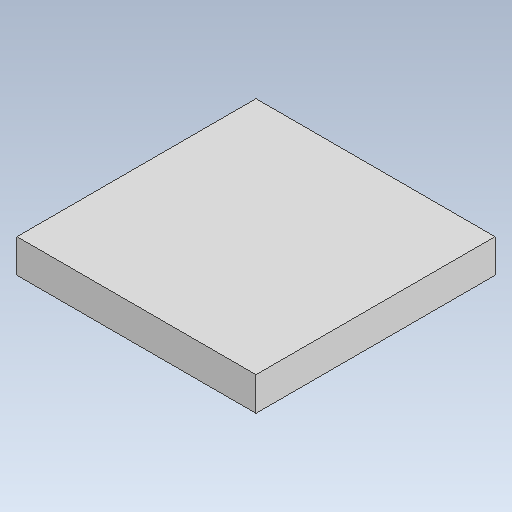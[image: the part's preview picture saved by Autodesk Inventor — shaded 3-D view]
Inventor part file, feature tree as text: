
AUTODESK INVENTOR PART (.ipt)
format: ipt  version: 2021.1 (Build 251245000, 245)  size: 143,872 bytes
history: native  units: mm
features: extrude x3, sketch x3, fillet x2
ambient origin geometry x8: Origin, YZ Plane, XZ Plane, XY Plane, X Axis, Y Axis, Z Axis, Center Point
bodies: Solid1 (feature_tree)
feature tree (8):
  extrude  "Extrusion1"  Depth=2.0mm TaperAngle=0.0deg
  extrude  "Extrusion2"  Depth=0.3mm
  extrude  "Extrusion3"  [1 undecoded]
  fillet  "Fillet1"  [1 undecoded]
  fillet  "Fillet2"  [1 undecoded]
  sketch  "Sketch1"  dims[d0=5.0mm d1=0.0mm d2=2.0mm d3=0.0mm]
  sketch  "Sketch2"  dims[d9=3.9mm d10=0.0mm d11=0.3mm]
  sketch  "Sketch3"  dims[d18=1.5mm]
note: 3 required parameter values undecoded (feature->parameter linkage not recoverable at this tier; creation-order binding heuristic only, values carry confidence <= 0.55)
